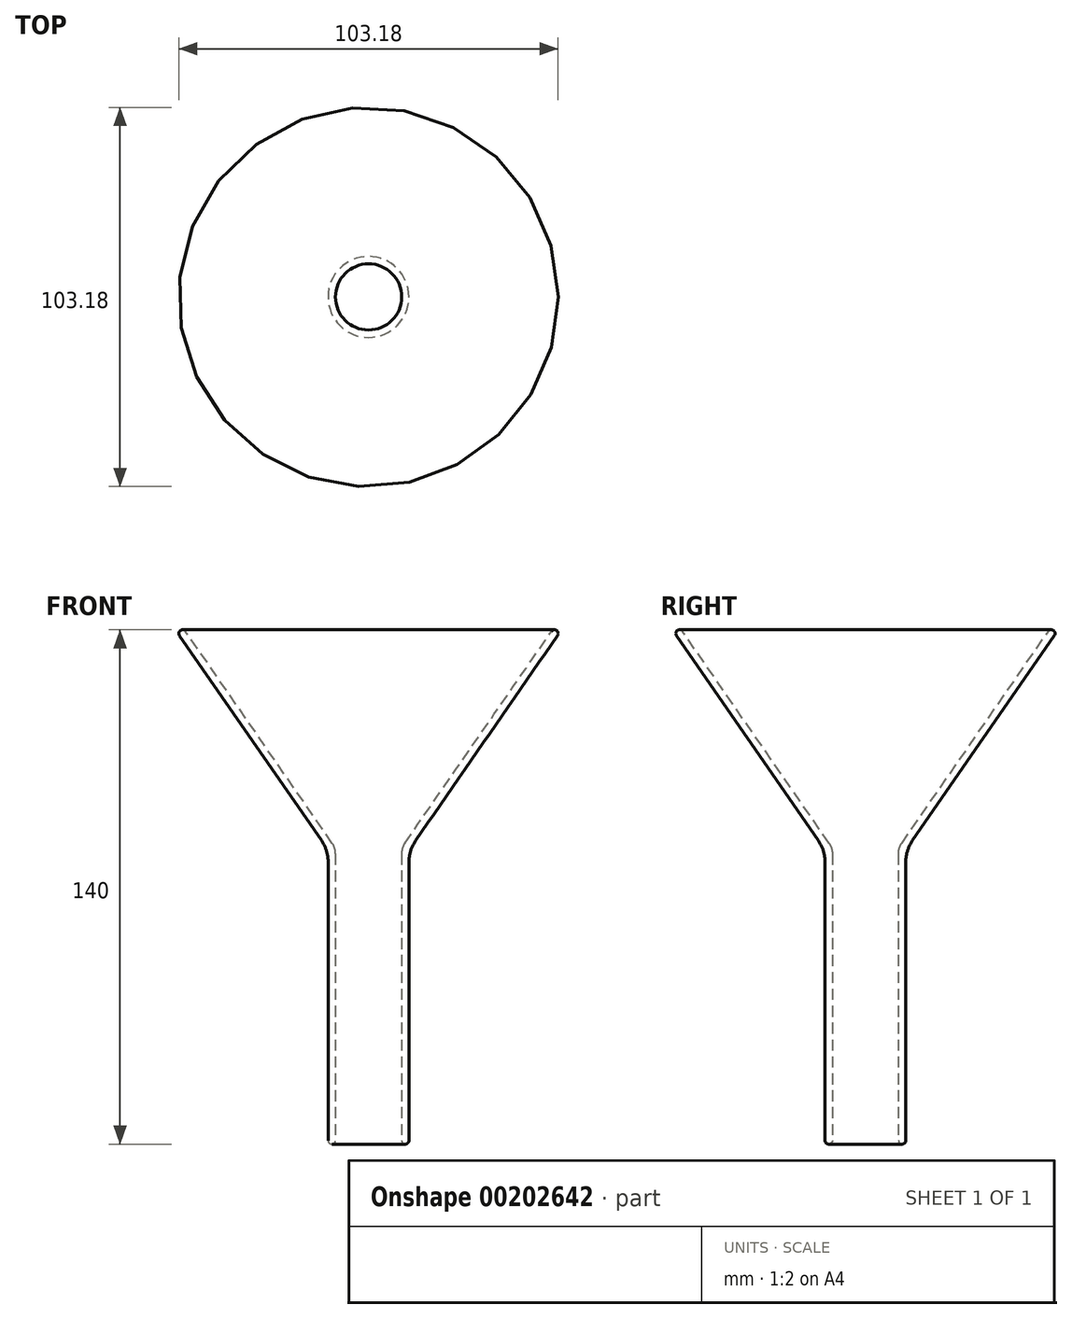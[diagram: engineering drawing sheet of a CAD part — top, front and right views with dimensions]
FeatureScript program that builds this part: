
annotation { "Feature Type Name" : "Feature", "Feature Type Description" : "" }
export const myFeature = defineFeature(function(context is Context, id is Id, definition is map)
    precondition{}
    {
        {
            var Q0;
            Q0=qCreatedBy(makeId("Front.planeOp"),FACE);
            var sketch = newSketch(context, id + "F0", { "sketchPlane" : qUnion([Q0])});
            skLineSegment(sketch, "E0", {"start": v(0, 0) * mm, "end": v(0, 80) * mm, "construction": true});
            skLineSegment(sketch, "E1", {"start": v(0, 80) * mm, "end": v(0, 140) * mm, "construction": true});
            skLineSegment(sketch, "E2", {"start": v(0, 0) * mm, "end": v(-11, 0) * mm, "construction": true});
            skLineSegment(sketch, "E3", {"start": v(-11, 0) * mm, "end": v(-11, 80) * mm});
            skLineSegment(sketch, "E4", {"start": v(-11, 80) * mm, "end": v(-52.5, 140) * mm});
            skLineSegment(sketch, "E5.0", {"start": v(-9, 80.62) * mm, "end": v(-50.07, 140) * mm});
            skLineSegment(sketch, "E5.1", {"start": v(-9, 0) * mm, "end": v(-9, 80.62) * mm});
            skLineSegment(sketch, "E6", {"start": v(-52.5, 140) * mm, "end": v(-50.07, 140) * mm});
            skLineSegment(sketch, "E7", {"start": v(-50.07, 140) * mm, "end": v(0, 140) * mm, "construction": true});
            skLineSegment(sketch, "E8", {"start": v(-9, 0) * mm, "end": v(-11, 0) * mm});
            skSolve(sketch);
        }
        {
            var Q0;
            Q0=makeQuery(id+"F0.imprint","IMPRINT",FACE,{"disambiguationData":[TD([[makeQuery(id+"F0.imprint","IMPRINT",EDGE,{"derivedFrom":sQuery(id+"F0.wireOp",EDGE,"E3")}),-1.0]])]});
            var Q1;
            Q1=sQuery(id+"F0.wireOp",EDGE,"E0");
            revolve(context, id + "F1", {"entities" : qUnion([Q0]), "axis" : qUnion([Q1]), "revolveType" : RevolveType.FULL});
        }
        {
            var Q0;
            Q0=makeQuery(id+"F1.opRevolve","SWEPT_EDGE",EDGE,{"disambiguationData":[OSD([sQuery(id+"F0.wireOp",EDGE,"E4"),sQuery(id+"F0.wireOp",EDGE,"E6")])]});
            var Q1;
            Q1=makeQuery(id+"F1.opRevolve","SWEPT_EDGE",EDGE,{"disambiguationData":[OSD([sQuery(id+"F0.wireOp",EDGE,"E5.0"),sQuery(id+"F0.wireOp",EDGE,"E6")])]});
            var Q2;
            Q2=makeQuery(id+"F1.opRevolve","SWEPT_EDGE",EDGE,{"disambiguationData":[OSD([sQuery(id+"F0.wireOp",EDGE,"E3"),sQuery(id+"F0.wireOp",EDGE,"E8")])]});
            var Q3;
            Q3=makeQuery(id+"F1.opRevolve","SWEPT_EDGE",EDGE,{"disambiguationData":[OSD([sQuery(id+"F0.wireOp",EDGE,"E5.1"),sQuery(id+"F0.wireOp",EDGE,"E8")])]});
            fillet(context, id + "F2", {"entities" : qUnion([Q0, Q1, Q2, Q3]), "radius" : 1 * mm, "tangentPropagation" : true, "allowEdgeOverflow" : false});
        }
        {
            var Q0;
            Q0=makeQuery(id+"F1.opRevolve","SWEPT_EDGE",EDGE,{"disambiguationData":[OSD([sQuery(id+"F0.wireOp",EDGE,"E5.0"),sQuery(id+"F0.wireOp",EDGE,"E5.1")])]});
            fillet(context, id + "F3", {"entities" : qUnion([Q0]), "radius" : 5 * mm, "tangentPropagation" : true, "allowEdgeOverflow" : false});
        }
        {
            var Q0;
            Q0=makeQuery(id+"F1.opRevolve","SWEPT_EDGE",EDGE,{"disambiguationData":[OSD([sQuery(id+"F0.wireOp",EDGE,"E3"),sQuery(id+"F0.wireOp",EDGE,"E4")])]});
            fillet(context, id + "F4", {"entities" : qUnion([Q0]), "radius" : 10 * mm, "tangentPropagation" : true, "allowEdgeOverflow" : false});
        }
    });
